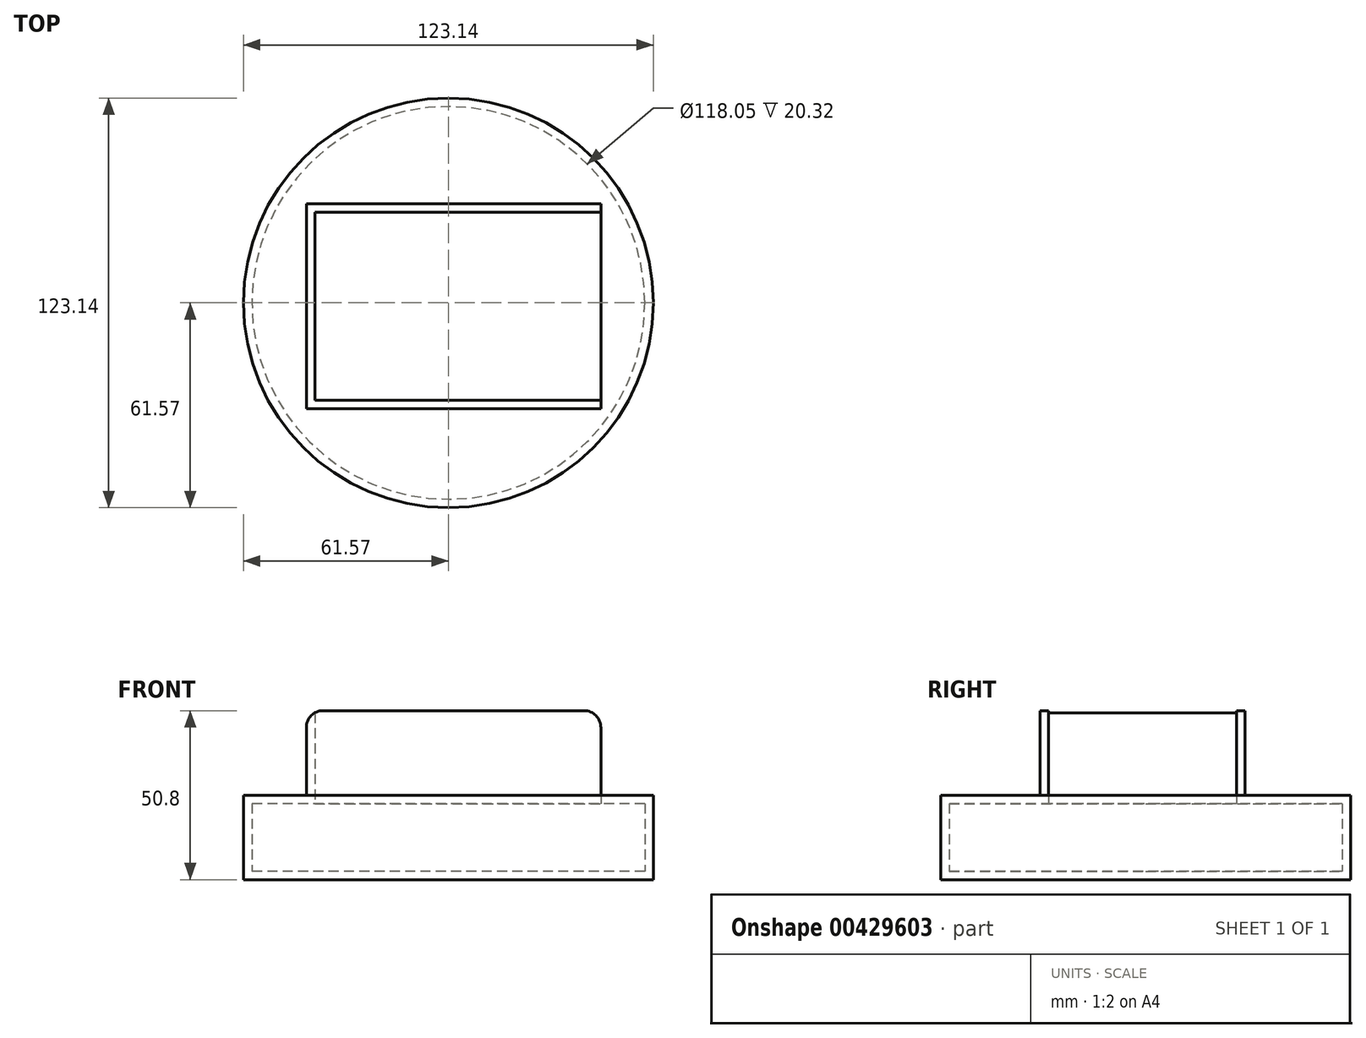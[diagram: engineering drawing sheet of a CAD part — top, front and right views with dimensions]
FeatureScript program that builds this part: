
annotation { "Feature Type Name" : "Feature", "Feature Type Description" : "" }
export const myFeature = defineFeature(function(context is Context, id is Id, definition is map)
    precondition{}
    {
        {
            var Q0;
            Q0=qCreatedBy(makeId("Top.planeOp"),FACE);
            var sketch = newSketch(context, id + "F0", { "sketchPlane" : qUnion([Q0])});
            skCircle(sketch, "E0", {"center": v(-52.39, 0) * mm, "radius": 61.57 * mm});
            skSolve(sketch);
        }
        {
            var Q0;
            Q0=makeQuery(id+"F0.imprint","IMPRINT",FACE,{"disambiguationData":[TD([[makeQuery(id+"F0.imprint","IMPRINT",EDGE,{"derivedFrom":sQuery(id+"F0.wireOp",EDGE,"E0")}),1.0]])]});
            extrude(context, id + "F1", {"entities" : qUnion([Q0]), "depth" : 25.4 * mm});
        }
        {
            var Q0;
            Q0=makeQuery(id+"F1.opExtrude","CAP_FACE",FACE,{"disambiguationData":[OSD([sQuery(id+"F0.wireOp",EDGE,"E0")])],"isStart":false});
            var sketch = newSketch(context, id + "F2", { "sketchPlane" : qUnion([Q0])});
            skLineSegment(sketch, "E1.bottom", {"start": v(-95.08, 29.82) * mm, "end": v(-6.55, 29.82) * mm});
            skLineSegment(sketch, "E1.top", {"start": v(-95.08, -31.78) * mm, "end": v(-6.55, -31.78) * mm});
            skLineSegment(sketch, "E1.left", {"start": v(-95.08, 29.82) * mm, "end": v(-95.08, -31.78) * mm});
            skLineSegment(sketch, "E1.right", {"start": v(-6.55, 29.82) * mm, "end": v(-6.55, -31.78) * mm});
            skSolve(sketch);
        }
        {
            var Q0;
            Q0 = qSketchRegion(id + "F2", true);
            extrude(context, id + "F3", {"entities" : qUnion([Q0]), "operationType" : NewBodyOperationType.ADD, "depth" : 25.4 * mm});
        }
        {
            var Q0;
            Q0=makeQuery(id+"F3.opExtrude","CAP_FACE",FACE,{"disambiguationData":[OSD([sQuery(id+"F2.wireOp",EDGE,"E1.bottom"),sQuery(id+"F2.wireOp",EDGE,"E1.top"),sQuery(id+"F2.wireOp",EDGE,"E1.left"),sQuery(id+"F2.wireOp",EDGE,"E1.right")])],"isStart":false});
            var Q1;
            Q1=makeQuery(id+"F3.opExtrude","SWEPT_FACE",FACE,{"disambiguationData":[OSD([sQuery(id+"F2.wireOp",EDGE,"E1.right")])]});
            shell(context, id + "F4", {"entities" : qUnion([Q0, Q1]), "thickness" : 2.54 * mm});
        }
        {
            var Q0;
            Q0=makeQuery(id+"F3.opExtrude","CAP_EDGE",EDGE,{"disambiguationData":[OSD([sQuery(id+"F2.wireOp",EDGE,"E1.left")])],"isStart":false});
            fillet(context, id + "F5", {"entities" : qUnion([Q0]), "radius" : 5.08 * mm, "tangentPropagation" : true, "allowEdgeOverflow" : false});
        }
        {
            var Q0;
            Q0=makeQuery(id+"F3.opExtrude","CAP_EDGE",EDGE,{"disambiguationData":[OSD([sQuery(id+"F2.wireOp",EDGE,"E1.right")])],"isStart":false});
            var Q1;
            {var subQ0=sQuery(id+"F2.wireOp",EDGE,"E1.right");Q1=makeQuery(id+"F4.opShell","OFFSET_EDGE",EDGE,{"disambiguationData":[OSD([subQ0]),TDD([makeQuery(id+"F3.opExtrude","CAP_EDGE",EDGE,{"disambiguationData":[OSD([subQ0])],"isStart":false})])]});}
            fillet(context, id + "F6", {"entities" : qUnion([Q0, Q1]), "radius" : 5.08 * mm, "tangentPropagation" : true, "allowEdgeOverflow" : false});
        }
    });
